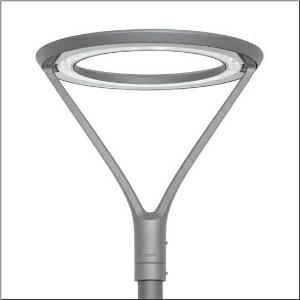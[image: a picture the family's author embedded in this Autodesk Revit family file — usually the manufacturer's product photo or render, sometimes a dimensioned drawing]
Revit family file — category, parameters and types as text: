
# Revit family: dl_r__20_led___pl1_2s_5xa512832s008p_7c07
name_source: partatom
category: Lighting Fixtures
units: mm (PartAtom-declared; Revit-internal decimal feet)

## family parameters
Cut with Voids When Loaded = No
Host = Face
Light Source = No
Part Type = Normal
Room Calculation Point = No
Round Connector Dimension = Use Diameter
Shared = No

## types (1)
- --- (1 x LED, 4330 lm, 51.4 W, 2200K)
    Apparent Load = 51 VA
    CIE Flux Codes = 34 78 98 100 100
    Color Rendering = 70
    Color Temperature = 2200K
    Default Elevation = 1800 mm
    Description = DL® 20 LED, mast luminaire, primary light control with reflector, highly specular, primary optical cover: cover, of toughened safety glass of clear glass with excellent transmission level, light distribution: PL1.2s, light emission: direct distribution, primary light characteristic: symmetric, installation type: post-top, LED, High Power LED, rated luminous flux: 4.210lm, luminous efficacy: 80lm/W, light colour: 722, colour temperature: 2200K, control gear: ECG Plus, control: flexible luminous flux parameterisation, time-dependent luminous flux control, constant luminous flux control, digital communication interface, power reduction, overheat protection, electronic power reduction, mains connection: 220..240V, 50/60Hz, connection cable pre-assembled, cable length: 5m, start of lifetime: 53W, end of lifetime: 54W, reduction: 24W, luminaire housing, upper part, of cast aluminium, powder-coated, Siteco® metallic grey (DB 702S), diameter: 690mm, height: 690mm, spigot size: 76mm (post-top), luminaire housing, of cast aluminium, powder-coated, Siteco® metallic grey (DB 702S), protection rating (complete): IP66, insulation class (complete): insulation class II (safety insulation), certification: CE, ENEC, VDE, impact resistance: IK08, permissible operating ambient temperature: -25..+30°C, standard-compliant lighting for roads and squares, packaging unit: 1 piece

Light Distribution: PL1.2s
    Height = 690 mm
    Lamp = 1 x LED
    Lamp Light Flux = 4330 lm
    Lamp Power = 51.4 W
    Lamp count = 1
    Length = 690 mm
    Luminous efficacy = 84 lm/W
    Manufacturer = Siteco
    ModVariant = No
    Model = 5XA512832S008P
    Number of Poles = 1
    OnlyDefault = Yes
    Power Factor = 1
    Product Name = DL® 20 LED | PL1.2s
    Product group = mast luminaire | pylon top
    ProductGroupID = 6100
    Protection Class = Protection class II
    Protection Degree = IP 66
    RLX_Detail_Level = 1
    RlxData = <blob elided: 204697 chars, md5=dbf2acd6>
    Socket = socket
    Standby Power = 0 W
    System Light Flux = 4330 lm
    System Power = 51 W
    Type Comments = factory setting: luminous flux: 100 % | dim-lin: 254 | 683 mA
    Type Image = l_1006001.jpg
    URL = http://relux.com
    VarID = @adj_118383
    Voltage = 0 V
    Weight = 0.00 kg
    Width = 0 mm  [stored 0 ft]

note: [stored X ft] marks values corroborated as IEEE doubles in the binary element streams (Revit-internal decimal feet)

## geometry (parser evidence)
native form markers: Blend x4, Sweep x9
no freeform markers — native parametric forms only
